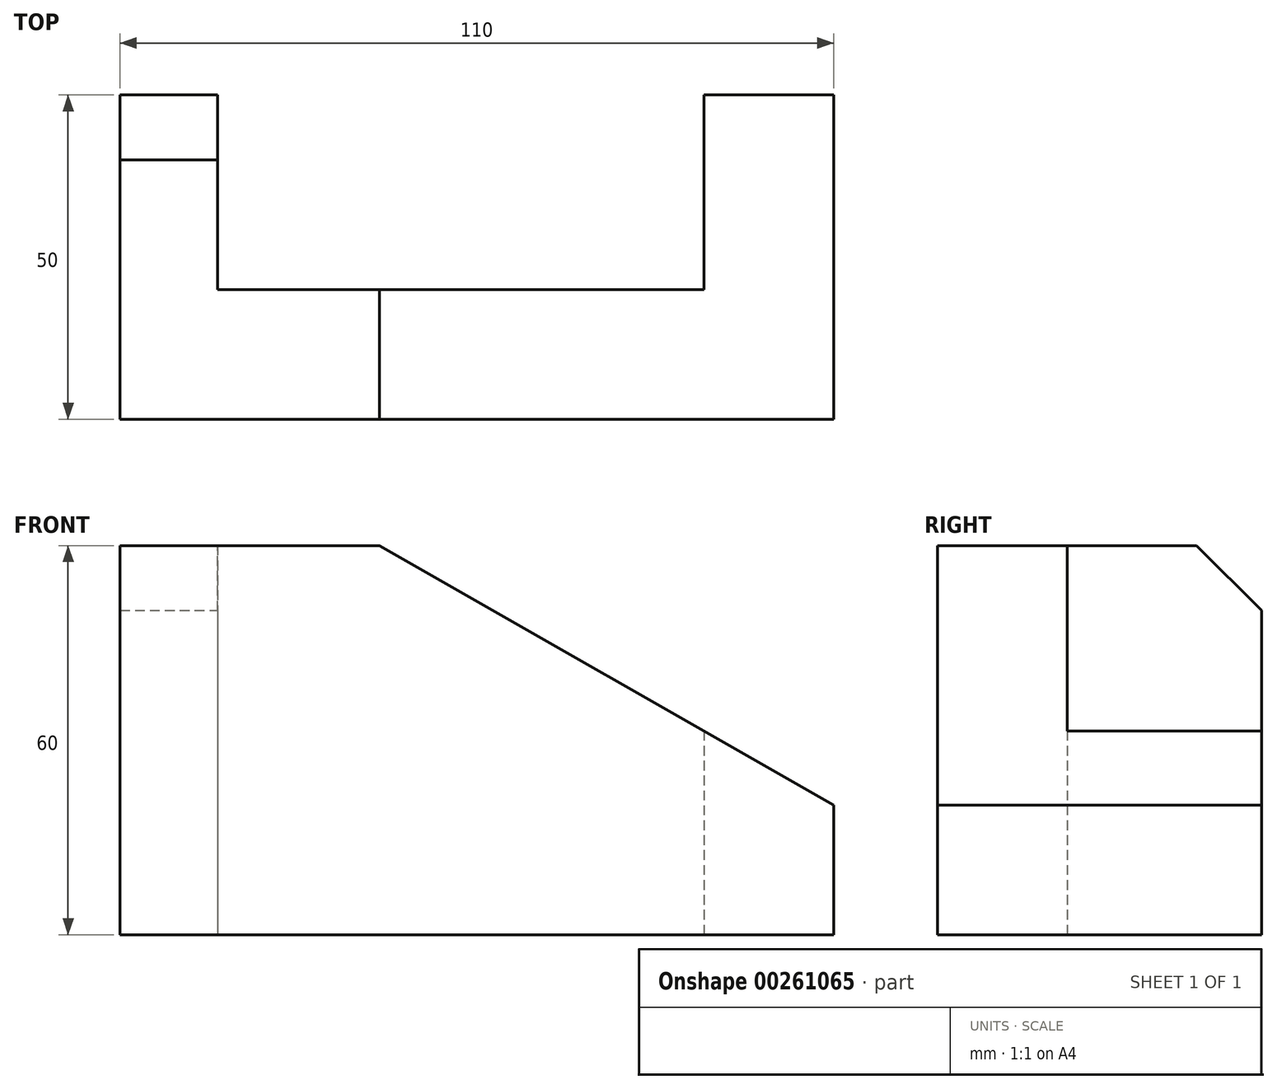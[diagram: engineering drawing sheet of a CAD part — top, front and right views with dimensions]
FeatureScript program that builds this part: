
annotation { "Feature Type Name" : "Feature", "Feature Type Description" : "" }
export const myFeature = defineFeature(function(context is Context, id is Id, definition is map)
    precondition{}
    {
        {
            var Q0;
            Q0=qCreatedBy(makeId("Front.planeOp"),FACE);
            var sketch = newSketch(context, id + "F0", { "sketchPlane" : qUnion([Q0])});
            skLineSegment(sketch, "E0", {"start": v(0, 0) * mm, "end": v(0, 60) * mm});
            skLineSegment(sketch, "E1", {"start": v(0, 60) * mm, "end": v(40, 60) * mm});
            skLineSegment(sketch, "E2", {"start": v(40, 60) * mm, "end": v(110, 20) * mm});
            skLineSegment(sketch, "E3", {"start": v(110, 20) * mm, "end": v(110, 0) * mm});
            skLineSegment(sketch, "E4", {"start": v(110, 0) * mm, "end": v(0, 0) * mm});
            skSolve(sketch);
        }
        {
            var Q0;
            Q0=makeQuery(id+"F0.imprint","IMPRINT",FACE,{"disambiguationData":[TD([[makeQuery(id+"F0.imprint","IMPRINT",EDGE,{"derivedFrom":sQuery(id+"F0.wireOp",EDGE,"E0")}),-1.0]])]});
            extrude(context, id + "F1", {"entities" : qUnion([Q0]), "depth" : 50 * mm});
        }
        {
            var Q0;
            Q0=qCreatedBy(makeId("Front.planeOp"),FACE);
            var sketch = newSketch(context, id + "F2", { "sketchPlane" : qUnion([Q0])});
            skLineSegment(sketch, "E5.bottom", {"start": v(15, 60.72) * mm, "end": v(90, 60.72) * mm});
            skLineSegment(sketch, "E5.top", {"start": v(15, -0.96) * mm, "end": v(90, -0.96) * mm});
            skLineSegment(sketch, "E5.left", {"start": v(15, 60.72) * mm, "end": v(15, -0.96) * mm});
            skLineSegment(sketch, "E5.right", {"start": v(90, 60.72) * mm, "end": v(90, -0.96) * mm});
            skSolve(sketch);
        }
        {
            var Q0;
            Q0=makeQuery(id+"F2.imprint","IMPRINT",FACE,{"disambiguationData":[TD([[makeQuery(id+"F2.imprint","IMPRINT",EDGE,{"derivedFrom":sQuery(id+"F2.wireOp",EDGE,"E5.bottom")}),-1.0]])]});
            extrude(context, id + "F3", {"entities" : qUnion([Q0]), "operationType" : NewBodyOperationType.REMOVE, "oppositeDirection" : true, "depth" : 30 * mm});
        }
        {
            var Q0;
            Q0 = qSketchRegion(id + "F2", true);
            extrude(context, id + "F4", {"entities" : qUnion([Q0]), "operationType" : NewBodyOperationType.REMOVE, "oppositeDirection" : true, "depth" : 30 * mm});
        }
        {
            var Q0;
            Q0 = qSketchRegion(id + "F2", true);
            extrude(context, id + "F5", {"entities" : qUnion([Q0]), "operationType" : NewBodyOperationType.REMOVE, "depth" : 30 * mm});
        }
        {
            var Q0;
            Q0=makeQuery(id+"F1.opExtrude","CAP_EDGE",EDGE,{"disambiguationData":[OSD([sQuery(id+"F0.wireOp",EDGE,"E1")])],"isStart":true});
            chamfer(context, id + "F6", {"entities" : qUnion([Q0]), "width" : 10 * mm, "tangentPropagation" : true});
        }
    });
